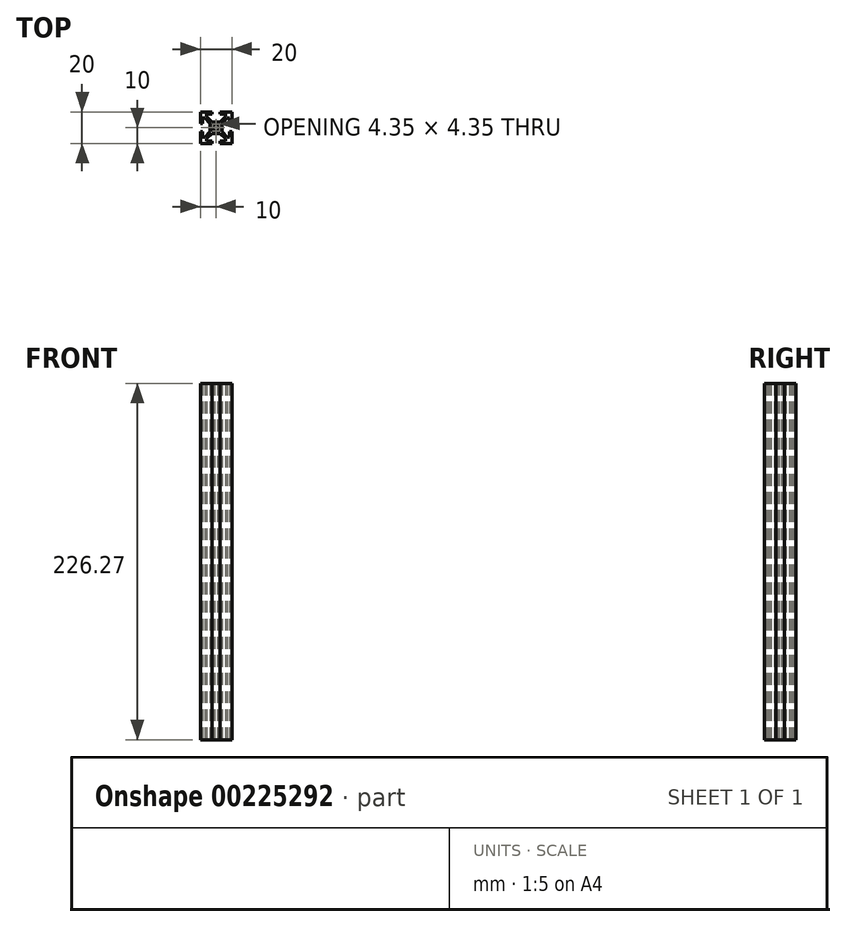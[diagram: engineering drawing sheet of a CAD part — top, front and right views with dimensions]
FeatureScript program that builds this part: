
annotation { "Feature Type Name" : "Feature", "Feature Type Description" : "" }
export const myFeature = defineFeature(function(context is Context, id is Id, definition is map)
    precondition{}
    {
        {
            var Q0;
            Q0=qCreatedBy(makeId("Top.planeOp"),FACE);
            var sketch = newSketch(context, id + "F0", { "sketchPlane" : qUnion([Q0])});
            skLineSegment(sketch, "E0.bottom", {"start": v(10, 10) * mm, "end": v(-10, 10) * mm});
            skLineSegment(sketch, "E0.top", {"start": v(10, -10) * mm, "end": v(-10, -10) * mm});
            skLineSegment(sketch, "E0.left", {"start": v(10, 10) * mm, "end": v(10, -10) * mm});
            skLineSegment(sketch, "E0.right", {"start": v(-10, 10) * mm, "end": v(-10, -10) * mm});
            skPoint(sketch, "E0.middle", {"position": v(0, 0) * mm});
            skLineSegment(sketch, "E1", {"start": v(-10, 10) * mm, "end": v(10, -10) * mm, "construction": true});
            skLineSegment(sketch, "E2", {"start": v(-10, -10) * mm, "end": v(10, 10) * mm, "construction": true});
            skLineSegment(sketch, "E3", {"start": v(0, 10) * mm, "end": v(0, -10) * mm, "construction": true});
            skLineSegment(sketch, "E4", {"start": v(-10, 0) * mm, "end": v(10, 0) * mm, "construction": true});
            skPoint(sketch, "E4.endSnap0", {"position": v(10, 0) * mm});
            skLineSegment(sketch, "E5", {"start": v(-2.63, 13.49) * mm, "end": v(2.63, 13.49) * mm});
            skLineSegment(sketch, "E6", {"start": v(2.63, 13.49) * mm, "end": v(2.63, 8.5) * mm});
            skLineSegment(sketch, "E7", {"start": v(2.63, 8.5) * mm, "end": v(6, 8.5) * mm});
            skLineSegment(sketch, "E8", {"start": v(6, 8.5) * mm, "end": v(6, 7.06) * mm});
            skLineSegment(sketch, "E9", {"start": v(6, 7.06) * mm, "end": v(2.6, 3.66) * mm});
            skLineSegment(sketch, "E10", {"start": v(2.6, 3.66) * mm, "end": v(-2.6, 3.66) * mm});
            skLineSegment(sketch, "E11", {"start": v(-2.6, 3.66) * mm, "end": v(-6, 7.06) * mm});
            skLineSegment(sketch, "E12", {"start": v(-6, 7.06) * mm, "end": v(-6, 8.5) * mm});
            skLineSegment(sketch, "E13", {"start": v(-6, 8.5) * mm, "end": v(-2.63, 8.5) * mm});
            skLineSegment(sketch, "E14", {"start": v(-2.63, 8.5) * mm, "end": v(-2.63, 13.49) * mm});
            skCircle(sketch, "E15", {"center": v(0, 0) * mm, "radius": 2.1 * mm});
            skLineSegment(sketch, "E16.MirrorCS", {"start": v(-7.06, 6) * mm, "end": v(-8.5, 6) * mm});
            skLineSegment(sketch, "E17.MirrorCS", {"start": v(-3.66, 2.6) * mm, "end": v(-7.06, 6) * mm});
            skLineSegment(sketch, "E18.MirrorCS", {"start": v(-8.5, 6) * mm, "end": v(-8.5, 2.63) * mm});
            skLineSegment(sketch, "E19.MirrorCS", {"start": v(-3.66, -2.6) * mm, "end": v(-3.66, 2.6) * mm});
            skLineSegment(sketch, "E20.MirrorCS", {"start": v(-7.06, -6) * mm, "end": v(-3.66, -2.6) * mm});
            skLineSegment(sketch, "E21.MirrorCS", {"start": v(-8.5, -6) * mm, "end": v(-7.06, -6) * mm});
            skLineSegment(sketch, "E22.MirrorCS", {"start": v(-8.5, -2.63) * mm, "end": v(-8.5, -6) * mm});
            skLineSegment(sketch, "E23.MirrorCS", {"start": v(-13.49, -2.63) * mm, "end": v(-8.5, -2.63) * mm});
            skLineSegment(sketch, "E24.MirrorCS", {"start": v(-13.49, 2.63) * mm, "end": v(-13.49, -2.63) * mm});
            skLineSegment(sketch, "E25.MirrorCS", {"start": v(-8.5, 2.63) * mm, "end": v(-13.49, 2.63) * mm});
            skLineSegment(sketch, "E26.MirrorCS", {"start": v(-2.6, -3.66) * mm, "end": v(-6, -7.06) * mm});
            skLineSegment(sketch, "E27.MirrorCS", {"start": v(2.6, -3.66) * mm, "end": v(-2.6, -3.66) * mm});
            skLineSegment(sketch, "E28.MirrorCS", {"start": v(6, -7.06) * mm, "end": v(2.6, -3.66) * mm});
            skLineSegment(sketch, "E29.MirrorCS", {"start": v(6, -8.5) * mm, "end": v(6, -7.06) * mm});
            skLineSegment(sketch, "E30.MirrorCS", {"start": v(2.63, -8.5) * mm, "end": v(6, -8.5) * mm});
            skLineSegment(sketch, "E31.MirrorCS", {"start": v(2.63, -13.49) * mm, "end": v(2.63, -8.5) * mm});
            skLineSegment(sketch, "E32.MirrorCS", {"start": v(-2.63, -13.49) * mm, "end": v(2.63, -13.49) * mm});
            skLineSegment(sketch, "E33.MirrorCS", {"start": v(-2.63, -8.5) * mm, "end": v(-2.63, -13.49) * mm});
            skLineSegment(sketch, "E34.MirrorCS", {"start": v(-6, -8.5) * mm, "end": v(-2.63, -8.5) * mm});
            skLineSegment(sketch, "E35.MirrorCS", {"start": v(-6, -7.06) * mm, "end": v(-6, -8.5) * mm});
            skLineSegment(sketch, "E36.MirrorCS", {"start": v(7.06, 6) * mm, "end": v(3.66, 2.6) * mm});
            skLineSegment(sketch, "E37.MirrorCS", {"start": v(8.5, 6) * mm, "end": v(7.06, 6) * mm});
            skLineSegment(sketch, "E38.MirrorCS", {"start": v(8.5, 2.63) * mm, "end": v(8.5, 6) * mm});
            skLineSegment(sketch, "E39.MirrorCS", {"start": v(13.49, 2.63) * mm, "end": v(8.5, 2.63) * mm});
            skLineSegment(sketch, "E40.MirrorCS", {"start": v(13.49, -2.63) * mm, "end": v(13.49, 2.63) * mm});
            skLineSegment(sketch, "E41.MirrorCS", {"start": v(8.5, -2.63) * mm, "end": v(13.49, -2.63) * mm});
            skLineSegment(sketch, "E42.MirrorCS", {"start": v(8.5, -6) * mm, "end": v(8.5, -2.63) * mm});
            skLineSegment(sketch, "E43.MirrorCS", {"start": v(7.06, -6) * mm, "end": v(8.5, -6) * mm});
            skLineSegment(sketch, "E44.MirrorCS", {"start": v(3.66, -2.6) * mm, "end": v(7.06, -6) * mm});
            skLineSegment(sketch, "E45.MirrorCS", {"start": v(3.66, 2.6) * mm, "end": v(3.66, -2.6) * mm});
            skCircle(sketch, "E46", {"center": v(-1.48, 1.48) * mm, "radius": 0.7 * mm});
            skCircle(sketch, "E47.MirrorC", {"center": v(1.48, 1.48) * mm, "radius": 0.7 * mm});
            skCircle(sketch, "E48.MirrorC", {"center": v(-1.48, -1.48) * mm, "radius": 0.7 * mm});
            skCircle(sketch, "E49.MirrorC", {"center": v(1.48, -1.48) * mm, "radius": 0.7 * mm});
            skSolve(sketch);
        }
        {
            var Q0;
            {var subQ29=sQuery(id+"F0.wireOp",EDGE,"E7");Q0=makeQuery(id+"F0.imprint","IMPRINT",FACE,{"disambiguationData":[TD([[makeQuery(id+"F0.imprint","IMPRINT",EDGE,{"derivedFrom":subQ29}),1.0]])]});}
            extrude(context, id + "F1", {"entities" : qUnion([Q0]), "depth" : 226.27 * mm});
        }
    });
